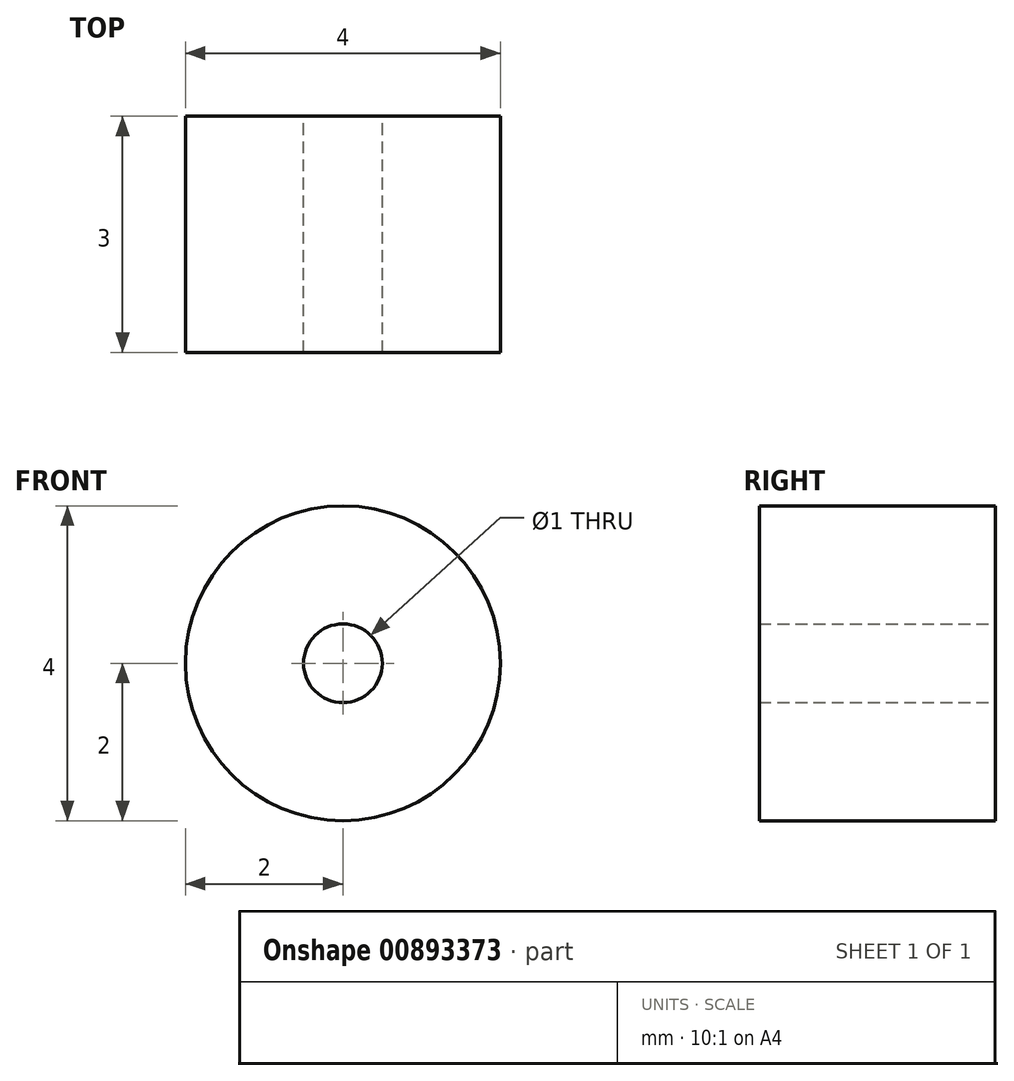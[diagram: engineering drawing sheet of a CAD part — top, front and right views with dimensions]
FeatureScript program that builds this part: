
annotation { "Feature Type Name" : "Feature", "Feature Type Description" : "" }
export const myFeature = defineFeature(function(context is Context, id is Id, definition is map)
    precondition{}
    {
        {
            var Q0;
            Q0=qCreatedBy(makeId("Front.planeOp"),FACE);
            var sketch = newSketch(context, id + "F0", { "sketchPlane" : qUnion([Q0])});
            skCircle(sketch, "E0", {"center": v(0, 0) * mm, "radius": 2 * mm});
            skCircle(sketch, "E1", {"center": v(0, 0) * mm, "radius": 0.5 * mm});
            skSolve(sketch);
        }
        {
            var Q0;
            Q0=makeQuery(id+"F0.imprint","IMPRINT",FACE,{"disambiguationData":[TD([[makeQuery(id+"F0.imprint","IMPRINT",EDGE,{"derivedFrom":sQuery(id+"F0.wireOp",EDGE,"E0")}),1.0]])]});
            extrude(context, id + "F1", {"entities" : qUnion([Q0]), "depth" : 3 * mm, "offsetDistance" : 25 * mm});
        }
    });
